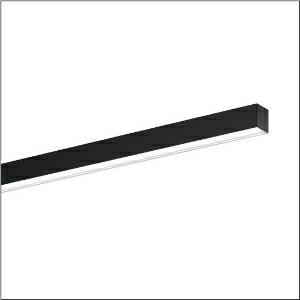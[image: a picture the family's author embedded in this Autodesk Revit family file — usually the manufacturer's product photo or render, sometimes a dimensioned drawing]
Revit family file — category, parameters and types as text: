
# Revit family: silica_21_51mx20da42bb
name_source: partatom
category: Lighting Fixtures
units: mm (PartAtom-declared; Revit-internal decimal feet)

## family parameters
Cut with Voids When Loaded = No
Host = Face
Light Source = No
Part Type = Normal
Room Calculation Point = No
Round Connector Dimension = Use Diameter
Shared = No

## types (1)
- --- (1 x LED, 2400 lm, 15.2 W, 4000K)
    Apparent Load = 15 VA
    CIE Flux Codes = 48 79 96 100 100
    Color Rendering = 80
    Color Temperature = 4000K
    Default Elevation = 1800 mm
    Description = Silica 21, office luminaire, primary optical cover: cover, of PMMA, opal, light emission: direct distribution, primary light characteristic: symmetric, installation type: surface-mounted, LED, rated luminous flux: 2.400lm, luminous efficacy: 158lm/W, light colour: 840, colour temperature: 4000K, control gear: DALI 2, with terminal, 3+2-pole, max. 2.5mm², mains connection: 220..240V, AC, 50/60Hz, rated input power: 15.2W, luminaire housing, of aluminium, matt jet black (RAL 9005), length: 1.204mm, width: 53mm, height: 53mm, protection rating (complete): IP20, insulation class (complete): insulation class I (protective earthing), certification: CE, permissible operating ambient temperature: 0..+35°C, standard: EN 50419, packaging unit: 1 piece
    Height = 53 mm
    Lamp = 1 x LED
    Lamp Light Flux = 2400 lm
    Lamp Power = 15.2 W
    Lamp count = 1
    Length = 1204 mm
    Luminous efficacy = 158 lm/W
    Manufacturer = Siteco
    ModVariant = No
    Model = 51MX20DA42BB
    Mounting Place = Ceiling
    Mounting Type = Surface mounted
    Number of Poles = 1
    OnlyDefault = Yes
    Power Factor = 1
    Product Name = Silica 21
    Product group = office luminaire | ceiling mounted
    ProductGroupID = 301
    Protection Class = Protection class I
    Protection Degree = IP 20
    RLX_Detail_Level = 1
    RLX_Emergency_Light_Flux = 0 lm
    RLX_Emergency_Type = 0
    RLX_Emergency_Type_DB = No
    RlxData = <blob elided: 28841 chars, md5=01376f7e>
    Socket = socket
    Standby Power = 0 W
    System Light Flux = 2400 lm
    System Power = 15 W
    Type Comments = factory setting: luminous flux: 100 % | dim-lin: 254 | 218 mA
    Type Image = l_1335925.jpg
    URL = http://relux.com
    VarID = @adj_027873
    Voltage = 0 V
    Weight = 0.00 kg
    Width = 53 mm

## geometry (parser evidence)
native form markers: Blend x4, Sweep x9
no freeform markers — native parametric forms only
